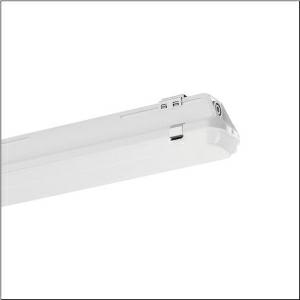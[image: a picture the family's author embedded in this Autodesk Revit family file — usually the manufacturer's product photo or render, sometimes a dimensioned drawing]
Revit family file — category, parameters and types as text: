
# Revit family: monsun_r__21_emergency_51fb10dp467b3h_4b81
name_source: partatom
category: Lighting Fixtures
units: mm (PartAtom-declared; Revit-internal decimal feet)

## family parameters
Cut with Voids When Loaded = No
Host = Face
Light Source = No
Part Type = Normal
Room Calculation Point = No
Round Connector Dimension = Use Diameter
Shared = No

## types (1)
- --- (1 x LED, 6060 lm, 42.2 W, 4000K)
    Apparent Load = 42 VA
    CIE Flux Codes = 47 77 93 94 100
    Color Rendering = 80
    Color Temperature = 4000K
    Default Elevation = 1800 mm
    Description = Monsun® 21 emergency, damp-proof luminaire, chain hanger, primary optical cover: enclosure, of PMMA, light emission: direct distribution, primary light characteristic: symmetric, installation type: vertical mounting, horizontal mounting, surface-mounted, suspended mounting, LED, rated luminous flux: 6.060lm, luminous efficacy: 144lm/W, light colour: 840, colour temperature: 4000K, control gear: ECG DALI, with terminal, 5+3-pole, max. 2.5mm², mains connection: 220..240V, AC, 50/60Hz, rated input power: 42W, control gear: single battery element, battery: NiCd, 4,5Ah, mains connection: 230V, housing, of glass-fibre reinforced polyester, uncoated, bright grey, length: 1.590mm, width: 90mm, height: 88mm, clip for enclosure, of stainless steel (V2A), ceiling mounting element, of stainless steel (V2A), chain hanger, of stainless steel (V2A), protection rating (complete): IP66, insulation class (complete): insulation class I (protective earthing), certification: CE, UKCA, protection symbol: D, impact resistance: IK04, permissible operating ambient temperature: +5..+25°C, standard: EN 60598-2-1, EN 50419, EN 60598-2-22, corresponds to IFS (International Featured Standards) requirements for safety and quality in the food industry, for indoor or canopied outdoor use, no direct snow, no direct sun, no direct rain, packaging unit: 1 piece
    Height = 89 mm
    Lamp = 1 x LED
    Lamp Light Flux = 6060 lm
    Lamp Power = 42.2 W
    Lamp count = 1
    Length = 1590 mm
    Luminous efficacy = 144 lm/W
    Manufacturer = Siteco
    ModVariant = No
    Model = 51FB10DP467B3H
    Mounting Place = Ceiling
    Mounting Type = Pendant
    Number of Poles = 1
    OnlyDefault = Yes
    Power Factor = 1
    Product Name = Monsun® 21 emergency
    Product group = damp-proof luminaire | ceiling pendant
    ProductGroupID = 908
    Protection Class = Protection class I
    Protection Degree = IP 66
    RLX_Detail_Level = 1
    RlxData = <blob elided: 92489 chars, md5=472986ca>
    Socket = socket
    Standby Power = 0 W
    System Light Flux = 6060 lm
    System Power = 42 W
    Type Comments = factory setting: luminous flux: 100 % | dim-lin: 254 | 261 mA
    Type Image = l_1006717.jpg
    URL = http://relux.com
    VarID = @adj_124873
    Voltage = 0 V
    Weight = 0.00 kg
    Width = 90 mm

## geometry (parser evidence)
native form markers: Blend x4, Sweep x12
no freeform markers — native parametric forms only
